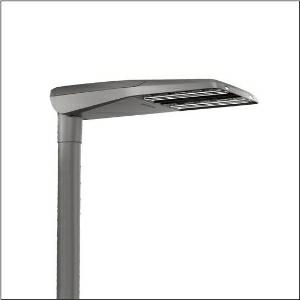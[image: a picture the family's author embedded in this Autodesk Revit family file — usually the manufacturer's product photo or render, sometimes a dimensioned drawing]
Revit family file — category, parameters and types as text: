
# Revit family: streetlight_sl_11_iq_midi___st1_2a_5xc3a51f08me_8c89
name_source: partatom
category: Lighting Fixtures
units: mm (PartAtom-declared; Revit-internal decimal feet)

## family parameters
Cut with Voids When Loaded = No
Host = Face
Light Source = No
Part Type = Normal
Room Calculation Point = No
Round Connector Dimension = Use Diameter
Shared = No

## types (1)
- --- (1 x LED, 18110 lm, 124.7 W, 3000K)
    Apparent Load = 125 VA
    CIE Flux Codes = 32 70 96 100 100
    Color Rendering = 70
    Color Temperature = 3000K
    Default Elevation = 1800 mm
    Description = Streetlight SL 11 iQ midi, mast luminaire, primary light control with 3 zone facetted reflector, of plastic, silver coated, highly specular, primary optical cover: cover, of PMMA, transparent, light distribution: ST1.2a, light emission: direct distribution, primary light characteristic: asymmetric, installation type: post-top, side-entry, LED, High Power LED, rated luminous flux: 18.110lm, luminous efficacy: 145lm/W, light colour: 730, colour temperature: 3000K, control: Street-Remote, optimised constant luminous flux control (CLO 2.0), Desk-Remote (wireless, voltage-free reading and setting of iQ features in the workshop via application-optimized NFC function/RFID function), Light-Fading, Smart-Wire, Night-Set, Lumen-Switch, Temp-Guard, Auto-Match, with cable H07RN-F 5x 1.5mm², mains connection: 220..240V, AC, 50/60Hz, connection cable pre-assembled, cable length: 12,5m, start of lifetime: 125W, end of lifetime: 132W, reduction: 57W, luminaire housing, of diecast aluminium, powder-coated, Siteco® metallic grey (DB 702S), length: 780mm, width: 376mm, height: 118mm, spigot size: 60/76mm (post-top) and 42/60/76mm (side-entry), mast flange for spigot size: 42mm: 5XC10008XM4, 60mm: 5XC10008XM2, 76/60mm: 5XC10108XM1, equipment: Power, protection rating (complete): IP66, insulation class (complete): insulation class II (safety insulation), certification: CE, ENEC, VDE, impact resistance: IK09, permissible operating ambient temperature for outdoor applications: -25..+50°C, standard-compliant lighting for roads and squares, packaging unit: 1 piece

Light Distribution: ST1.2a
    Height = 118 mm
    Lamp = 1 x LED
    Lamp Light Flux = 18110 lm
    Lamp Power = 124.7 W
    Lamp count = 1
    Length = 780 mm
    Luminous efficacy = 145 lm/W
    Manufacturer = Siteco
    ModVariant = No
    Model = 5XC3A51F08ME
    Number of Poles = 1
    OnlyDefault = Yes
    Power Factor = 1
    Product Name = Streetlight SL 11 iQ midi | ST1.2a
    Product group = mast luminaire | pylon top
    ProductGroupID = 6100
    Protection Class = Protection class II
    Protection Degree = IP 66
    RLX_Detail_Level = 1
    RlxData = <blob elided: 70381 chars, md5=c7d783fe>
    Socket = socket
    Standby Power = 0 W
    System Light Flux = 18110 lm
    System Power = 125 W
    Type Comments = factory setting: luminous flux: 100 % | dim-lin: 254 | 557 mA
    Type Image = l_1005960.jpg
    URL = http://relux.com
    VarID = @adj_118781
    Voltage = 0 V
    Weight = 0.00 kg
    Width = 376 mm

## geometry (parser evidence)
native form markers: Blend x4, Sweep x10
no freeform markers — native parametric forms only
